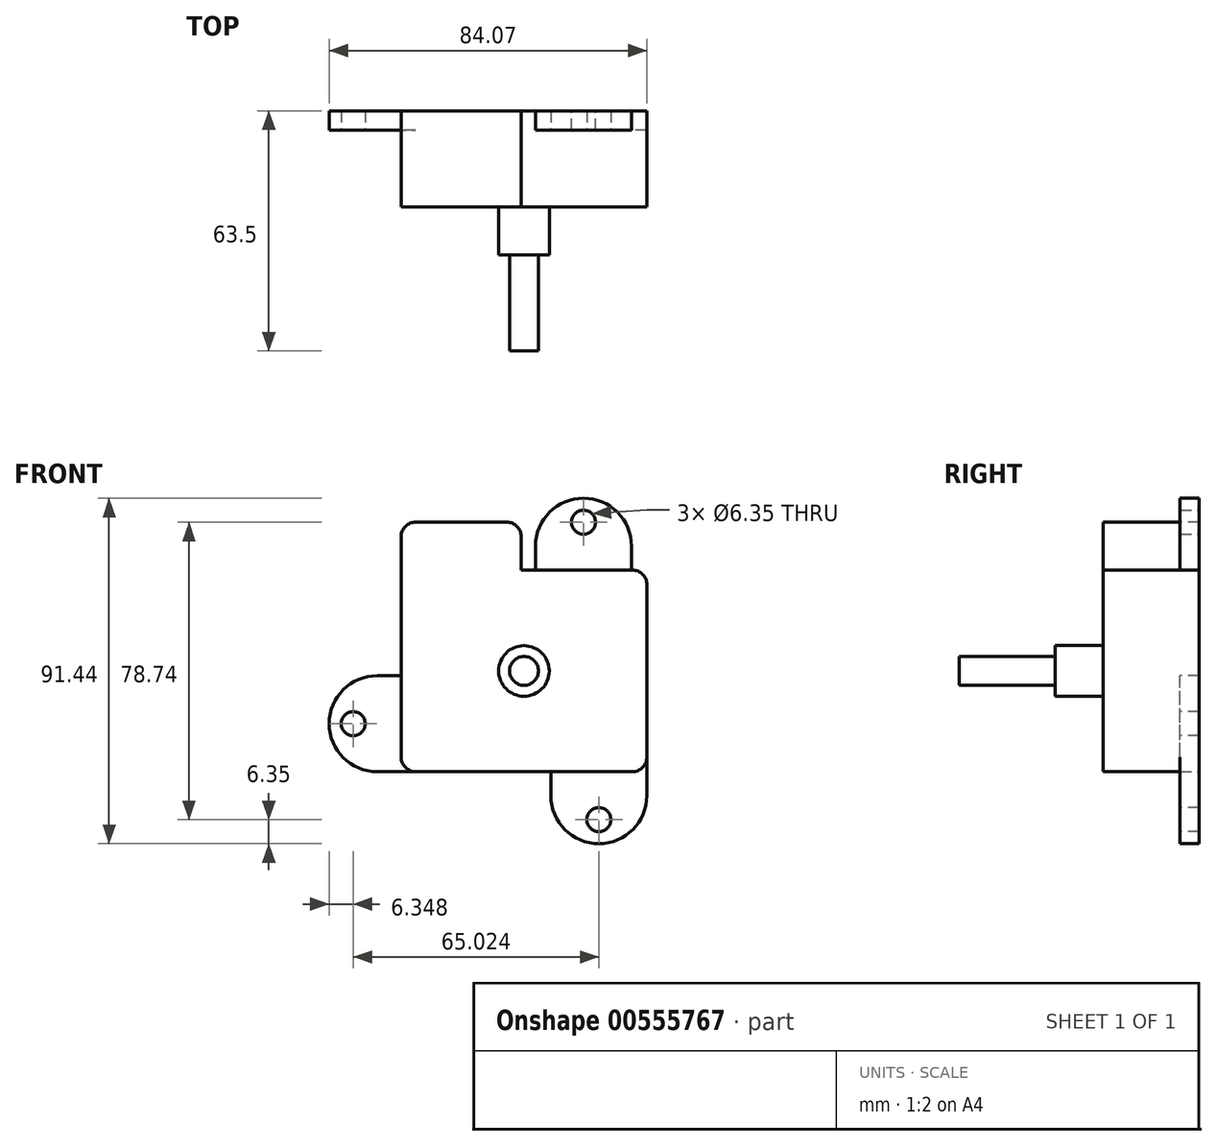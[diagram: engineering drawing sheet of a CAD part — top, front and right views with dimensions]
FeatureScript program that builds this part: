
annotation { "Feature Type Name" : "Feature", "Feature Type Description" : "" }
export const myFeature = defineFeature(function(context is Context, id is Id, definition is map)
    precondition{}
    {
        {
            var Q0;
            Q0=qCreatedBy(makeId("Front.planeOp"),FACE);
            var sketch = newSketch(context, id + "F0", { "sketchPlane" : qUnion([Q0])});
            skLineSegment(sketch, "E0.bottom", {"start": v(32.51, -26.67) * mm, "end": v(-32.51, -26.67) * mm});
            skLineSegment(sketch, "E0.top", {"start": v(32.51, 26.67) * mm, "end": v(-32.51, 26.67) * mm});
            skLineSegment(sketch, "E0.left", {"start": v(32.51, -26.67) * mm, "end": v(32.51, 26.67) * mm});
            skLineSegment(sketch, "E0.right", {"start": v(-32.51, -26.67) * mm, "end": v(-32.51, 26.67) * mm});
            skPoint(sketch, "E0.middle", {"position": v(0, 0) * mm});
            skSolve(sketch);
        }
        {
            var Q0;
            Q0 = qSketchRegion(id + "F0", true);
            extrude(context, id + "F1", {"entities" : qUnion([Q0]), "depth" : 12.7 * mm, "offsetDistance" : 25.4 * mm, "hasSecondDirection" : true, "secondDirectionOppositeDirection" : true, "secondDirectionDepth" : 12.7 * mm});
        }
        {
            var Q0;
            Q0=makeQuery(id+"F1.opExtrude","CAP_FACE",FACE,{"disambiguationData":[OSD([sQuery(id+"F0.wireOp",EDGE,"E0.bottom"),sQuery(id+"F0.wireOp",EDGE,"E0.top"),sQuery(id+"F0.wireOp",EDGE,"E0.left"),sQuery(id+"F0.wireOp",EDGE,"E0.right")])],"isStart":false});
            var sketch = newSketch(context, id + "F2", { "sketchPlane" : qUnion([Q0])});
            skLineSegment(sketch, "E1.bottom", {"start": v(-32.51, 26.67) * mm, "end": v(-0.76, 26.67) * mm});
            skLineSegment(sketch, "E1.top", {"start": v(-32.51, 39.37) * mm, "end": v(-0.76, 39.37) * mm});
            skLineSegment(sketch, "E1.left", {"start": v(-32.51, 26.67) * mm, "end": v(-32.51, 39.37) * mm});
            skLineSegment(sketch, "E1.right", {"start": v(-0.76, 26.67) * mm, "end": v(-0.76, 39.37) * mm});
            skSolve(sketch);
        }
        {
            var Q0;
            Q0 = qSketchRegion(id + "F2", true);
            extrude(context, id + "F3", {"entities" : qUnion([Q0]), "operationType" : NewBodyOperationType.ADD, "oppositeDirection" : true, "depth" : 25.4 * mm, "offsetDistance" : 25.4 * mm});
        }
        {
            var Q0;
            Q0=makeQuery(id+"F3.boolean.opBoolean","MERGE",FACE,{"derivedFrom":[makeQuery(id+"F1.opExtrude","CAP_FACE",FACE,{"disambiguationData":[OSD([sQuery(id+"F0.wireOp",EDGE,"E0.bottom"),sQuery(id+"F0.wireOp",EDGE,"E0.top"),sQuery(id+"F0.wireOp",EDGE,"E0.left"),sQuery(id+"F0.wireOp",EDGE,"E0.right")])],"isStart":true}),makeQuery(id+"F3.opExtrude","CAP_FACE",FACE,{"disambiguationData":[OSD([sQuery(id+"F2.wireOp",EDGE,"E1.bottom"),sQuery(id+"F2.wireOp",EDGE,"E1.top"),sQuery(id+"F2.wireOp",EDGE,"E1.left"),sQuery(id+"F2.wireOp",EDGE,"E1.right")])],"isStart":false})]});
            var sketch = newSketch(context, id + "F4", { "sketchPlane" : qUnion([Q0])});
            skLineSegment(sketch, "E2.bottom", {"start": v(-3.05, 26.67) * mm, "end": v(-28.45, 26.67) * mm});
            skLineSegment(sketch, "E2.top", {"start": v(-28.45, 33.02) * mm, "end": v(-3.05, 33.02) * mm});
            skLineSegment(sketch, "E2.left", {"start": v(-28.45, 26.67) * mm, "end": v(-28.45, 33.02) * mm});
            skLineSegment(sketch, "E2.right", {"start": v(-3.05, 26.67) * mm, "end": v(-3.05, 33.02) * mm});
            skSolve(sketch);
        }
        {
            var Q0;
            Q0 = qSketchRegion(id + "F4", true);
            extrude(context, id + "F5", {"entities" : qUnion([Q0]), "operationType" : NewBodyOperationType.ADD, "oppositeDirection" : true, "depth" : 5.08 * mm, "offsetDistance" : 25.4 * mm});
        }
        {
            var Q0;
            Q0=makeQuery(id+"F5.boolean.opBoolean","MERGE",FACE,{"derivedFrom":[makeQuery(id+"F3.boolean.opBoolean","MERGE",FACE,{"derivedFrom":[makeQuery(id+"F1.opExtrude","CAP_FACE",FACE,{"disambiguationData":[OSD([sQuery(id+"F0.wireOp",EDGE,"E0.bottom"),sQuery(id+"F0.wireOp",EDGE,"E0.top"),sQuery(id+"F0.wireOp",EDGE,"E0.left"),sQuery(id+"F0.wireOp",EDGE,"E0.right")])],"isStart":true}),makeQuery(id+"F3.opExtrude","CAP_FACE",FACE,{"disambiguationData":[OSD([sQuery(id+"F2.wireOp",EDGE,"E1.bottom"),sQuery(id+"F2.wireOp",EDGE,"E1.top"),sQuery(id+"F2.wireOp",EDGE,"E1.left"),sQuery(id+"F2.wireOp",EDGE,"E1.right")])],"isStart":false})]}),makeQuery(id+"F5.opExtrude","CAP_FACE",FACE,{"disambiguationData":[OSD([sQuery(id+"F4.wireOp",EDGE,"E2.bottom"),sQuery(id+"F4.wireOp",EDGE,"E2.top"),sQuery(id+"F4.wireOp",EDGE,"E2.left"),sQuery(id+"F4.wireOp",EDGE,"E2.right")])],"isStart":true})]});
            var sketch = newSketch(context, id + "F6", { "sketchPlane" : qUnion([Q0])});
            skArc(sketch, "E3", {"start": v(-3.05, 33.02) * mm, "mid": v(-15.75, 45.72) * mm, "end": v(-28.45, 33.02) * mm});
            skSolve(sketch);
        }
        {
            var Q0;
            Q0=makeQuery(id+"F5.opExtrude","SWEPT_FACE",FACE,{"disambiguationData":[OSD([sQuery(id+"F4.wireOp",EDGE,"E2.top")])]});
            var sketch = newSketch(context, id + "F7", { "sketchPlane" : qUnion([Q0])});
            skLineSegment(sketch, "E4.bottom", {"start": v(15.75, 12.7) * mm, "end": v(28.45, 12.7) * mm});
            skLineSegment(sketch, "E4.top", {"start": v(15.75, 7.62) * mm, "end": v(28.45, 7.62) * mm});
            skLineSegment(sketch, "E4.left", {"start": v(15.75, 12.7) * mm, "end": v(15.75, 7.62) * mm});
            skLineSegment(sketch, "E4.right", {"start": v(28.45, 12.7) * mm, "end": v(28.45, 7.62) * mm});
            skSolve(sketch);
        }
        {
            var Q0;
            Q0=makeQuery(id+"F7.imprint","IMPRINT",FACE,{"disambiguationData":[TD([[makeQuery(id+"F7.imprint","IMPRINT",EDGE,{"derivedFrom":sQuery(id+"F7.wireOp",EDGE,"E4.bottom")}),1.0]])]});
            var Q1;
            Q1=sQuery(id+"F7.wireOp",EDGE,"E4.left");
            revolve(context, id + "F8", {"operationType" : NewBodyOperationType.ADD, "surfaceOperationType" : NewSurfaceOperationType.NEW, "entities" : qUnion([Q0]), "axis" : qUnion([Q1]), "revolveType" : RevolveType.ONE_DIRECTION, "angle" : 180 * degree});
        }
        {
            var Q0;
            Q0=makeQuery(id+"F6.imprint","IMPRINT",FACE,{"disambiguationData":[TD([[makeQuery(id+"F6.imprint","IMPRINT",EDGE,{"derivedFrom":sQuery(id+"F6.wireOp",EDGE,"E3")}),1.0]])]});
            var sketch = newSketch(context, id + "F9", { "sketchPlane" : qUnion([Q0])});
            skCircle(sketch, "E5", {"center": v(-15.75, 39.37) * mm, "radius": 3.17 * mm});
            skSolve(sketch);
        }
        {
            var Q0;
            Q0 = qSketchRegion(id + "F9", true);
            extrude(context, id + "F10", {"entities" : qUnion([Q0]), "operationType" : NewBodyOperationType.REMOVE, "oppositeDirection" : true, "depth" : 25.4 * mm, "offsetDistance" : 25.4 * mm});
        }
        {
            var Q0;
            Q0=makeQuery(id+"F3.boolean.opBoolean","MERGE",FACE,{"derivedFrom":[makeQuery(id+"F1.opExtrude","SWEPT_FACE",FACE,{"disambiguationData":[OSD([sQuery(id+"F0.wireOp",EDGE,"E0.right")])]}),makeQuery(id+"F3.opExtrude","SWEPT_FACE",FACE,{"disambiguationData":[OSD([sQuery(id+"F2.wireOp",EDGE,"E1.left")])]})]});
            var sketch = newSketch(context, id + "F11", { "sketchPlane" : qUnion([Q0])});
            skLineSegment(sketch, "E6.bottom", {"start": v(-12.7, -26.67) * mm, "end": v(-7.62, -26.67) * mm});
            skLineSegment(sketch, "E6.top", {"start": v(-12.7, -1.27) * mm, "end": v(-7.62, -1.27) * mm});
            skLineSegment(sketch, "E6.left", {"start": v(-12.7, -26.67) * mm, "end": v(-12.7, -1.27) * mm});
            skLineSegment(sketch, "E6.right", {"start": v(-7.62, -26.67) * mm, "end": v(-7.62, -1.27) * mm});
            skSolve(sketch);
        }
        {
            var Q0;
            Q0 = qSketchRegion(id + "F11", true);
            extrude(context, id + "F12", {"entities" : qUnion([Q0]), "operationType" : NewBodyOperationType.ADD, "depth" : 6.35 * mm, "offsetDistance" : 25.4 * mm});
        }
        {
            var Q0;
            Q0=makeQuery(id+"F12.opExtrude","CAP_FACE",FACE,{"disambiguationData":[OSD([sQuery(id+"F11.wireOp",EDGE,"E6.bottom"),sQuery(id+"F11.wireOp",EDGE,"E6.top"),sQuery(id+"F11.wireOp",EDGE,"E6.left"),sQuery(id+"F11.wireOp",EDGE,"E6.right")])],"isStart":false});
            var sketch = newSketch(context, id + "F13", { "sketchPlane" : qUnion([Q0])});
            skLineSegment(sketch, "E7.bottom", {"start": v(-12.7, -1.27) * mm, "end": v(-7.62, -1.27) * mm});
            skLineSegment(sketch, "E7.top", {"start": v(-12.7, -13.97) * mm, "end": v(-7.62, -13.97) * mm});
            skLineSegment(sketch, "E7.left", {"start": v(-12.7, -1.27) * mm, "end": v(-12.7, -13.97) * mm});
            skLineSegment(sketch, "E7.right", {"start": v(-7.62, -1.27) * mm, "end": v(-7.62, -13.97) * mm});
            skSolve(sketch);
        }
        {
            var Q0;
            Q0 = qSketchRegion(id + "F13", true);
            var Q1;
            Q1=sQuery(id+"F13.wireOp",EDGE,"E7.top");
            revolve(context, id + "F14", {"operationType" : NewBodyOperationType.ADD, "surfaceOperationType" : NewSurfaceOperationType.NEW, "entities" : qUnion([Q0]), "axis" : qUnion([Q1]), "revolveType" : RevolveType.FULL});
        }
        {
            var Q0;
            Q0=makeQuery(id+"F14.boolean.opBoolean","MERGE",FACE,{"derivedFrom":[makeQuery(id+"F12.opExtrude","SWEPT_FACE",FACE,{"disambiguationData":[OSD([sQuery(id+"F11.wireOp",EDGE,"E6.right")])]}),makeQuery(id+"F14.opRevolve","SWEPT_FACE",FACE,{"disambiguationData":[OSD([sQuery(id+"F13.wireOp",EDGE,"E7.right")])]})]});
            var sketch = newSketch(context, id + "F15", { "sketchPlane" : qUnion([Q0])});
            skCircle(sketch, "E8", {"center": v(-45.21, -13.97) * mm, "radius": 3.18 * mm});
            skSolve(sketch);
        }
        {
            var Q0;
            Q0 = qSketchRegion(id + "F15", true);
            extrude(context, id + "F16", {"entities" : qUnion([Q0]), "operationType" : NewBodyOperationType.REMOVE, "oppositeDirection" : true, "depth" : 25.4 * mm, "offsetDistance" : 25.4 * mm});
        }
        {
            var Q0;
            Q0=makeQuery(id+"F12.boolean.opBoolean","MERGE",FACE,{"derivedFrom":[makeQuery(id+"F1.opExtrude","SWEPT_FACE",FACE,{"disambiguationData":[OSD([sQuery(id+"F0.wireOp",EDGE,"E0.bottom")])]}),makeQuery(id+"F12.opExtrude","SWEPT_FACE",FACE,{"disambiguationData":[OSD([sQuery(id+"F11.wireOp",EDGE,"E6.bottom")])]})]});
            var sketch = newSketch(context, id + "F17", { "sketchPlane" : qUnion([Q0])});
            skLineSegment(sketch, "E9.bottom", {"start": v(32.51, -12.7) * mm, "end": v(7.11, -12.7) * mm});
            skLineSegment(sketch, "E9.top", {"start": v(32.51, -7.62) * mm, "end": v(7.11, -7.62) * mm});
            skLineSegment(sketch, "E9.left", {"start": v(32.51, -12.7) * mm, "end": v(32.51, -7.62) * mm});
            skLineSegment(sketch, "E9.right", {"start": v(7.11, -12.7) * mm, "end": v(7.11, -7.62) * mm});
            skSolve(sketch);
        }
        {
            var Q0;
            Q0 = qSketchRegion(id + "F17", true);
            extrude(context, id + "F18", {"entities" : qUnion([Q0]), "operationType" : NewBodyOperationType.ADD, "depth" : 6.35 * mm, "offsetDistance" : 25.4 * mm});
        }
        {
            var Q0;
            Q0=makeQuery(id+"F18.opExtrude","CAP_FACE",FACE,{"disambiguationData":[OSD([sQuery(id+"F17.wireOp",EDGE,"E9.bottom"),sQuery(id+"F17.wireOp",EDGE,"E9.top"),sQuery(id+"F17.wireOp",EDGE,"E9.left"),sQuery(id+"F17.wireOp",EDGE,"E9.right")])],"isStart":false});
            var sketch = newSketch(context, id + "F19", { "sketchPlane" : qUnion([Q0])});
            skLineSegment(sketch, "E10.bottom", {"start": v(7.11, -12.7) * mm, "end": v(19.81, -12.7) * mm});
            skLineSegment(sketch, "E10.top", {"start": v(7.11, -7.62) * mm, "end": v(19.81, -7.62) * mm});
            skLineSegment(sketch, "E10.left", {"start": v(7.11, -12.7) * mm, "end": v(7.11, -7.62) * mm});
            skLineSegment(sketch, "E10.right", {"start": v(19.81, -12.7) * mm, "end": v(19.81, -7.62) * mm});
            skSolve(sketch);
        }
        {
            var Q0;
            Q0 = qSketchRegion(id + "F19", true);
            var Q1;
            Q1=sQuery(id+"F19.wireOp",EDGE,"E10.right");
            revolve(context, id + "F20", {"operationType" : NewBodyOperationType.ADD, "surfaceOperationType" : NewSurfaceOperationType.NEW, "entities" : qUnion([Q0]), "axis" : qUnion([Q1]), "revolveType" : RevolveType.FULL});
        }
        {
            var Q0;
            Q0=makeQuery(id+"F20.boolean.opBoolean","MERGE",FACE,{"derivedFrom":[makeQuery(id+"F18.opExtrude","SWEPT_FACE",FACE,{"disambiguationData":[OSD([sQuery(id+"F17.wireOp",EDGE,"E9.top")])]}),makeQuery(id+"F20.opRevolve","SWEPT_FACE",FACE,{"disambiguationData":[OSD([sQuery(id+"F19.wireOp",EDGE,"E10.top")])]})]});
            var sketch = newSketch(context, id + "F21", { "sketchPlane" : qUnion([Q0])});
            skCircle(sketch, "E11", {"center": v(19.81, -39.37) * mm, "radius": 3.18 * mm});
            skSolve(sketch);
        }
        {
            var Q0;
            Q0 = qSketchRegion(id + "F21", true);
            extrude(context, id + "F22", {"entities" : qUnion([Q0]), "operationType" : NewBodyOperationType.REMOVE, "oppositeDirection" : true, "depth" : 25.4 * mm, "offsetDistance" : 25.4 * mm});
        }
        {
            var Q0;
            Q0=makeQuery(id+"F3.opExtrude","SWEPT_EDGE",EDGE,{"disambiguationData":[OSD([sQuery(id+"F2.wireOp",EDGE,"E1.top"),sQuery(id+"F2.wireOp",EDGE,"E1.right")])]});
            var Q1;
            Q1=makeQuery(id+"F3.opExtrude","SWEPT_EDGE",EDGE,{"disambiguationData":[OSD([sQuery(id+"F2.wireOp",EDGE,"E1.top"),sQuery(id+"F2.wireOp",EDGE,"E1.left")])]});
            var Q2;
            Q2=makeQuery(id+"F1.opExtrude","SWEPT_EDGE",EDGE,{"disambiguationData":[OSD([sQuery(id+"F0.wireOp",EDGE,"E0.top"),sQuery(id+"F0.wireOp",EDGE,"E0.left")])]});
            var Q3;
            Q3=makeQuery(id+"F1.opExtrude","SWEPT_EDGE",EDGE,{"disambiguationData":[OSD([sQuery(id+"F0.wireOp",EDGE,"E0.bottom"),sQuery(id+"F0.wireOp",EDGE,"E0.left")])]});
            var Q4;
            Q4=makeQuery(id+"F1.opExtrude","SWEPT_EDGE",EDGE,{"disambiguationData":[OSD([sQuery(id+"F0.wireOp",EDGE,"E0.bottom"),sQuery(id+"F0.wireOp",EDGE,"E0.right")])]});
            fillet(context, id + "F23", {"entities" : qUnion([Q0, Q1, Q2, Q3, Q4]), "radius" : 3.8 * mm, "tangentPropagation" : true, "allowEdgeOverflow" : false});
        }
        {
            var Q0;
            Q0=makeQuery(id+"F3.boolean.opBoolean","MERGE",FACE,{"derivedFrom":[makeQuery(id+"F1.opExtrude","CAP_FACE",FACE,{"disambiguationData":[OSD([sQuery(id+"F0.wireOp",EDGE,"E0.bottom"),sQuery(id+"F0.wireOp",EDGE,"E0.top"),sQuery(id+"F0.wireOp",EDGE,"E0.left"),sQuery(id+"F0.wireOp",EDGE,"E0.right")])],"isStart":false}),makeQuery(id+"F3.opExtrude","CAP_FACE",FACE,{"disambiguationData":[OSD([sQuery(id+"F2.wireOp",EDGE,"E1.bottom"),sQuery(id+"F2.wireOp",EDGE,"E1.top"),sQuery(id+"F2.wireOp",EDGE,"E1.left"),sQuery(id+"F2.wireOp",EDGE,"E1.right")])],"isStart":true})]});
            var sketch = newSketch(context, id + "F24", { "sketchPlane" : qUnion([Q0])});
            skCircle(sketch, "E12", {"center": v(0, 0) * mm, "radius": 6.7 * mm});
            skCircle(sketch, "E13", {"center": v(0, 0) * mm, "radius": 2.54 * mm});
            skSolve(sketch);
        }
        {
            var Q0;
            Q0=makeQuery(id+"F24.imprint","IMPRINT",FACE,{"disambiguationData":[TD([[makeQuery(id+"F24.imprint","IMPRINT",EDGE,{"derivedFrom":sQuery(id+"F24.wireOp",EDGE,"E12")}),1.0]])]});
            extrude(context, id + "F25", {"entities" : qUnion([Q0]), "operationType" : NewBodyOperationType.ADD, "depth" : 12.7 * mm, "offsetDistance" : 25.4 * mm});
        }
        {
            var Q0;
            Q0=makeQuery(id+"F25.boolean.opBoolean","SPLIT",FACE,{"disambiguationData":[TD([makeQuery(id+"F25.opExtrude","SWEPT_FACE",FACE,{"disambiguationData":[OSD([sQuery(id+"F24.wireOp",EDGE,"E13")])]})])],"derivedFrom":makeQuery(id+"F3.boolean.opBoolean","MERGE",FACE,{"derivedFrom":[makeQuery(id+"F1.opExtrude","CAP_FACE",FACE,{"disambiguationData":[OSD([sQuery(id+"F0.wireOp",EDGE,"E0.bottom"),sQuery(id+"F0.wireOp",EDGE,"E0.top"),sQuery(id+"F0.wireOp",EDGE,"E0.left"),sQuery(id+"F0.wireOp",EDGE,"E0.right")])],"isStart":false}),makeQuery(id+"F3.opExtrude","CAP_FACE",FACE,{"disambiguationData":[OSD([sQuery(id+"F2.wireOp",EDGE,"E1.bottom"),sQuery(id+"F2.wireOp",EDGE,"E1.top"),sQuery(id+"F2.wireOp",EDGE,"E1.left"),sQuery(id+"F2.wireOp",EDGE,"E1.right")])],"isStart":true})]})});
            var sketch = newSketch(context, id + "F26", { "sketchPlane" : qUnion([Q0])});
            skCircle(sketch, "E14", {"center": v(0, 0) * mm, "radius": 3.8 * mm});
            skSolve(sketch);
        }
        {
            var Q0;
            Q0 = qSketchRegion(id + "F26", true);
            extrude(context, id + "F27", {"entities" : qUnion([Q0]), "operationType" : NewBodyOperationType.ADD, "depth" : 38.1 * mm, "offsetDistance" : 25.4 * mm});
        }
    });
